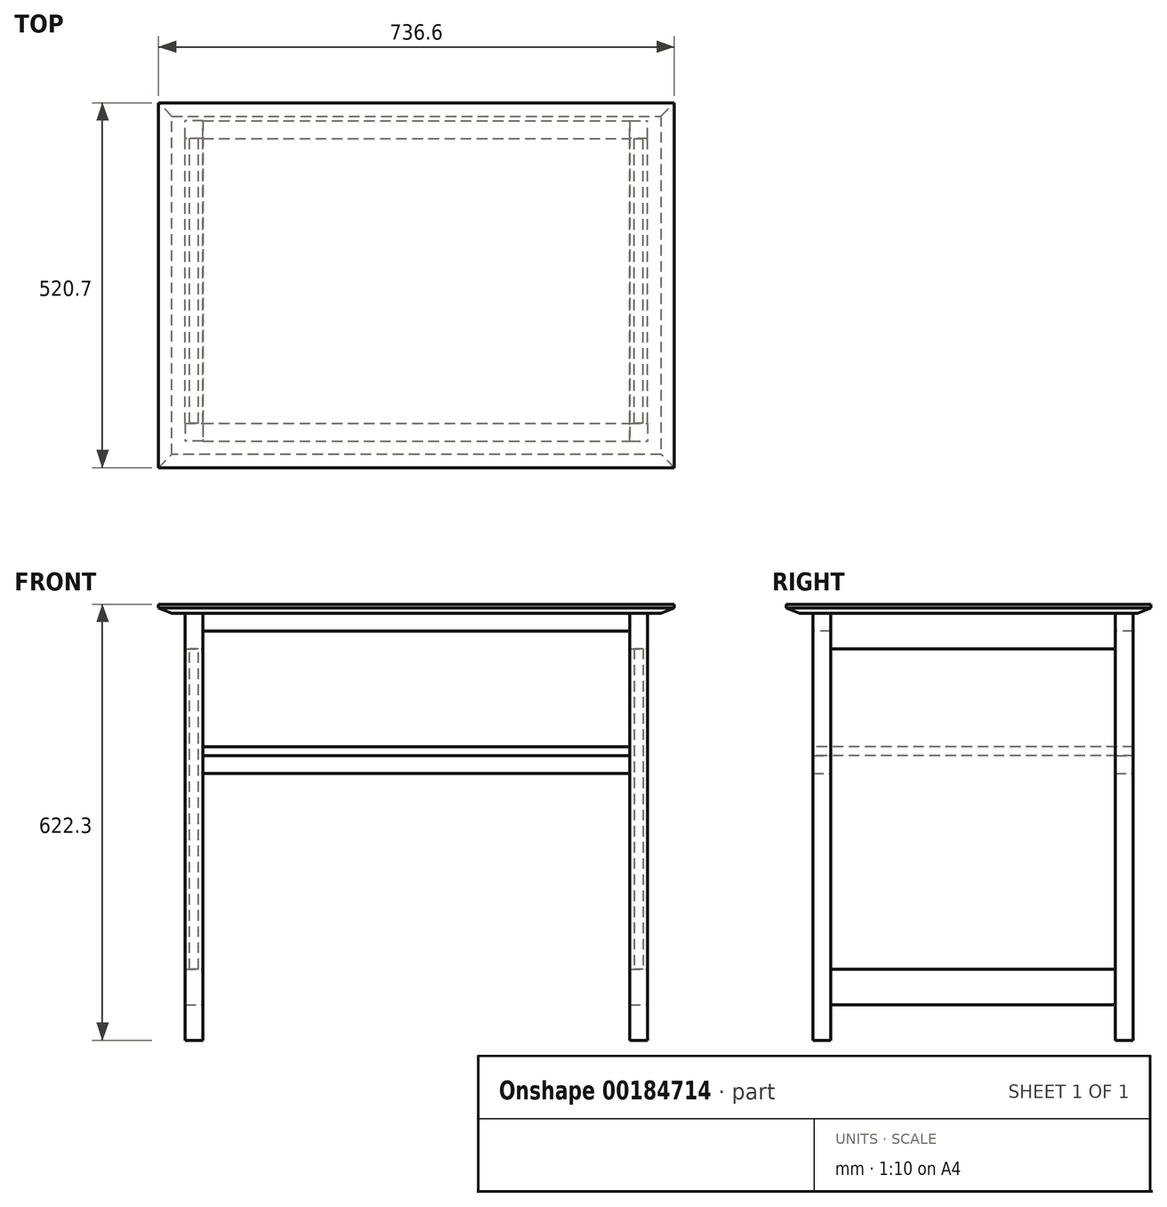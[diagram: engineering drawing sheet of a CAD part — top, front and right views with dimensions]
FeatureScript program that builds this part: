
annotation { "Feature Type Name" : "Feature", "Feature Type Description" : "" }
export const myFeature = defineFeature(function(context is Context, id is Id, definition is map)
    precondition{}
    {
        {
            var Q0;
            Q0=qCreatedBy(makeId("Top.planeOp"),FACE);
            var sketch = newSketch(context, id + "F0", { "sketchPlane" : qUnion([Q0])});
            skLineSegment(sketch, "E0.bottom", {"start": v(-304.8, 203.2) * mm, "end": v(304.8, 203.2) * mm});
            skLineSegment(sketch, "E0.top", {"start": v(-304.8, -203.2) * mm, "end": v(304.8, -203.2) * mm});
            skLineSegment(sketch, "E0.left", {"start": v(-304.8, 203.2) * mm, "end": v(-304.8, -203.2) * mm});
            skLineSegment(sketch, "E0.right", {"start": v(304.8, 203.2) * mm, "end": v(304.8, -203.2) * mm});
            skPoint(sketch, "E0.middle", {"position": v(0, 0) * mm});
            skLineSegment(sketch, "E1", {"start": v(0, 0) * mm, "end": v(0, 203.2) * mm});
            skLineSegment(sketch, "E2", {"start": v(0, 0) * mm, "end": v(-304.8, 0) * mm});
            skLineSegment(sketch, "E3.bottom", {"start": v(-304.8, 203.2) * mm, "end": v(-330.2, 203.2) * mm});
            skLineSegment(sketch, "E3.top", {"start": v(-304.8, 228.6) * mm, "end": v(-330.2, 228.6) * mm});
            skLineSegment(sketch, "E3.left", {"start": v(-304.8, 203.2) * mm, "end": v(-304.8, 228.6) * mm});
            skLineSegment(sketch, "E3.right", {"start": v(-330.2, 203.2) * mm, "end": v(-330.2, 228.6) * mm});
            skPoint(sketch, "E3.middle", {"position": v(-317.5, 215.9) * mm});
            skLineSegment(sketch, "E4.MirrorCS", {"start": v(330.2, 203.2) * mm, "end": v(330.2, 228.6) * mm});
            skPoint(sketch, "E5.MirrorP", {"position": v(317.5, 215.9) * mm});
            skLineSegment(sketch, "E6.MirrorCS", {"start": v(304.8, 203.2) * mm, "end": v(330.2, 203.2) * mm});
            skLineSegment(sketch, "E7.MirrorCS", {"start": v(304.8, 203.2) * mm, "end": v(304.8, 228.6) * mm});
            skLineSegment(sketch, "E8.MirrorCS", {"start": v(304.8, 228.6) * mm, "end": v(330.2, 228.6) * mm});
            skPoint(sketch, "E9.MirrorP", {"position": v(-317.5, -215.9) * mm});
            skLineSegment(sketch, "E10.MirrorCS", {"start": v(304.8, -203.2) * mm, "end": v(304.8, -228.6) * mm});
            skLineSegment(sketch, "E11.MirrorCS", {"start": v(304.8, -203.2) * mm, "end": v(330.2, -203.2) * mm});
            skLineSegment(sketch, "E12.MirrorCS", {"start": v(304.8, -228.6) * mm, "end": v(330.2, -228.6) * mm});
            skLineSegment(sketch, "E13.MirrorCS", {"start": v(-304.8, -228.6) * mm, "end": v(-330.2, -228.6) * mm});
            skLineSegment(sketch, "E14.MirrorCS", {"start": v(330.2, -203.2) * mm, "end": v(330.2, -228.6) * mm});
            skLineSegment(sketch, "E15.MirrorCS", {"start": v(-304.8, -203.2) * mm, "end": v(-304.8, -228.6) * mm});
            skLineSegment(sketch, "E16.MirrorCS", {"start": v(-304.8, -203.2) * mm, "end": v(-330.2, -203.2) * mm});
            skLineSegment(sketch, "E17.MirrorCS", {"start": v(-330.2, -203.2) * mm, "end": v(-330.2, -228.6) * mm});
            skPoint(sketch, "E18.MirrorP", {"position": v(317.5, -215.9) * mm});
            skSolve(sketch);
        }
        {
            var Q0;
            Q0=makeQuery(id+"F0.imprint","IMPRINT",FACE,{"disambiguationData":[TD([[makeQuery(id+"F0.imprint","IMPRINT",EDGE,{"derivedFrom":sQuery(id+"F0.wireOp",EDGE,"E3.bottom")}),-1.0]])]});
            var Q1;
            Q1=makeQuery(id+"F0.imprint","IMPRINT",FACE,{"disambiguationData":[TD([[makeQuery(id+"F0.imprint","IMPRINT",EDGE,{"derivedFrom":sQuery(id+"F0.wireOp",EDGE,"E4.MirrorCS")}),1.0]])]});
            var Q2;
            Q2=makeQuery(id+"F0.imprint","IMPRINT",FACE,{"disambiguationData":[TD([[makeQuery(id+"F0.imprint","IMPRINT",EDGE,{"derivedFrom":sQuery(id+"F0.wireOp",EDGE,"E10.MirrorCS")}),1.0]])]});
            var Q3;
            Q3=makeQuery(id+"F0.imprint","IMPRINT",FACE,{"disambiguationData":[TD([[makeQuery(id+"F0.imprint","IMPRINT",EDGE,{"derivedFrom":sQuery(id+"F0.wireOp",EDGE,"E13.MirrorCS")}),-1.0]])]});
            extrude(context, id + "F1", {"entities" : qUnion([Q0, Q1, Q2, Q3]), "depth" : 609.6 * mm});
        }
        {
            var Q0;
            Q0=makeQuery(id+"F1.opExtrude","SWEPT_FACE",FACE,{"disambiguationData":[OSD([sQuery(id+"F0.wireOp",EDGE,"E3.bottom")])]});
            var sketch = newSketch(context, id + "F2", { "sketchPlane" : qUnion([Q0])});
            skLineSegment(sketch, "E19.bottom", {"start": v(-330.2, 609.6) * mm, "end": v(-304.8, 609.6) * mm});
            skLineSegment(sketch, "E19.top", {"start": v(-330.2, 558.8) * mm, "end": v(-304.8, 558.8) * mm});
            skLineSegment(sketch, "E19.left", {"start": v(-330.2, 609.6) * mm, "end": v(-330.2, 558.8) * mm});
            skLineSegment(sketch, "E19.right", {"start": v(-304.8, 609.6) * mm, "end": v(-304.8, 558.8) * mm});
            skLineSegment(sketch, "E20.bottom", {"start": v(-330.2, 50.8) * mm, "end": v(-304.8, 50.8) * mm});
            skLineSegment(sketch, "E20.top", {"start": v(-330.2, 101.6) * mm, "end": v(-304.8, 101.6) * mm});
            skLineSegment(sketch, "E20.left", {"start": v(-330.2, 50.8) * mm, "end": v(-330.2, 101.6) * mm});
            skLineSegment(sketch, "E20.right", {"start": v(-304.8, 50.8) * mm, "end": v(-304.8, 101.6) * mm});
            skLineSegment(sketch, "E21", {"start": v(0, 0) * mm, "end": v(0, 145.1) * mm});
            skLineSegment(sketch, "E22.MirrorCS", {"start": v(330.2, 609.6) * mm, "end": v(304.8, 609.6) * mm});
            skLineSegment(sketch, "E23.MirrorCS", {"start": v(330.2, 50.8) * mm, "end": v(304.8, 50.8) * mm});
            skLineSegment(sketch, "E24.MirrorCS", {"start": v(330.2, 558.8) * mm, "end": v(304.8, 558.8) * mm});
            skLineSegment(sketch, "E25.MirrorCS", {"start": v(330.2, 101.6) * mm, "end": v(304.8, 101.6) * mm});
            skLineSegment(sketch, "E26.MirrorCS", {"start": v(304.8, 609.6) * mm, "end": v(304.8, 558.8) * mm});
            skLineSegment(sketch, "E27.MirrorCS", {"start": v(304.8, 50.8) * mm, "end": v(304.8, 101.6) * mm});
            skLineSegment(sketch, "E28.MirrorCS", {"start": v(330.2, 609.6) * mm, "end": v(330.2, 558.8) * mm});
            skLineSegment(sketch, "E29.MirrorCS", {"start": v(330.2, 50.8) * mm, "end": v(330.2, 101.6) * mm});
            skSolve(sketch);
        }
        {
            var Q0;
            Q0=makeQuery(id+"F2.imprint","IMPRINT",FACE,{"disambiguationData":[TD([[makeQuery(id+"F2.imprint","IMPRINT",EDGE,{"derivedFrom":sQuery(id+"F2.wireOp",EDGE,"E19.bottom")}),1.0]])]});
            var Q1;
            Q1=makeQuery(id+"F2.imprint","IMPRINT",FACE,{"disambiguationData":[TD([[makeQuery(id+"F2.imprint","IMPRINT",EDGE,{"derivedFrom":sQuery(id+"F2.wireOp",EDGE,"E22.MirrorCS")}),1.0]])]});
            var Q2;
            Q2=makeQuery(id+"F2.imprint","IMPRINT",FACE,{"disambiguationData":[TD([[makeQuery(id+"F2.imprint","IMPRINT",EDGE,{"derivedFrom":sQuery(id+"F2.wireOp",EDGE,"E23.MirrorCS")}),-1.0]])]});
            var Q3;
            Q3=makeQuery(id+"F2.imprint","IMPRINT",FACE,{"disambiguationData":[TD([[makeQuery(id+"F2.imprint","IMPRINT",EDGE,{"derivedFrom":sQuery(id+"F2.wireOp",EDGE,"E20.bottom")}),1.0]])]});
            extrude(context, id + "F3", {"entities" : qUnion([Q0, Q1, Q2, Q3]), "endBound" : BoundingType.UP_TO_NEXT, "depth" : 25.4 * mm});
        }
        {
            var Q0;
            Q0=makeQuery(id+"F1.opExtrude","SWEPT_FACE",FACE,{"disambiguationData":[OSD([sQuery(id+"F0.wireOp",EDGE,"E3.bottom")])]});
            var sketch = newSketch(context, id + "F4", { "sketchPlane" : qUnion([Q0])});
            skLineSegment(sketch, "E30.bottom", {"start": v(-311.15, 101.6) * mm, "end": v(-323.85, 101.6) * mm});
            skLineSegment(sketch, "E30.top", {"start": v(-311.15, 558.8) * mm, "end": v(-323.85, 558.8) * mm});
            skLineSegment(sketch, "E30.left", {"start": v(-311.15, 101.6) * mm, "end": v(-311.15, 558.8) * mm});
            skLineSegment(sketch, "E30.right", {"start": v(-323.85, 101.6) * mm, "end": v(-323.85, 558.8) * mm});
            skPoint(sketch, "E30.middle", {"position": v(-317.5, 330.2) * mm});
            skLineSegment(sketch, "E31", {"start": v(0, 0) * mm, "end": v(0, 207.5) * mm});
            skLineSegment(sketch, "E32.MirrorCS", {"start": v(311.15, 101.6) * mm, "end": v(323.85, 101.6) * mm});
            skLineSegment(sketch, "E33.MirrorCS", {"start": v(311.15, 558.8) * mm, "end": v(323.85, 558.8) * mm});
            skLineSegment(sketch, "E34.MirrorCS", {"start": v(323.85, 101.6) * mm, "end": v(323.85, 558.8) * mm});
            skLineSegment(sketch, "E35.MirrorCS", {"start": v(311.15, 101.6) * mm, "end": v(311.15, 558.8) * mm});
            skPoint(sketch, "E36.MirrorP", {"position": v(317.5, 330.2) * mm});
            skSolve(sketch);
        }
        {
            var Q0;
            Q0=makeQuery(id+"F4.imprint","IMPRINT",FACE,{"disambiguationData":[TD([[makeQuery(id+"F4.imprint","IMPRINT",EDGE,{"derivedFrom":sQuery(id+"F4.wireOp",EDGE,"E32.MirrorCS")}),1.0]])]});
            var Q1;
            Q1=makeQuery(id+"F4.imprint","IMPRINT",FACE,{"disambiguationData":[TD([[makeQuery(id+"F4.imprint","IMPRINT",EDGE,{"derivedFrom":sQuery(id+"F4.wireOp",EDGE,"E30.bottom")}),-1.0]])]});
            extrude(context, id + "F5", {"entities" : qUnion([Q0, Q1]), "endBound" : BoundingType.UP_TO_NEXT, "depth" : 25.4 * mm});
        }
        {
            var Q0;
            Q0=makeQuery(id+"F1.opExtrude","SWEPT_FACE",FACE,{"disambiguationData":[OSD([sQuery(id+"F0.wireOp",EDGE,"E10.MirrorCS")])]});
            var sketch = newSketch(context, id + "F6", { "sketchPlane" : qUnion([Q0])});
            skLineSegment(sketch, "E37.bottom", {"start": v(203.2, 406.4) * mm, "end": v(228.6, 406.4) * mm});
            skLineSegment(sketch, "E37.top", {"start": v(203.2, 381) * mm, "end": v(228.6, 381) * mm});
            skLineSegment(sketch, "E37.left", {"start": v(203.2, 406.4) * mm, "end": v(203.2, 381) * mm});
            skLineSegment(sketch, "E37.right", {"start": v(228.6, 406.4) * mm, "end": v(228.6, 381) * mm});
            skLineSegment(sketch, "E38.bottom", {"start": v(-203.2, 381) * mm, "end": v(-228.6, 381) * mm});
            skLineSegment(sketch, "E38.top", {"start": v(-203.2, 406.4) * mm, "end": v(-228.6, 406.4) * mm});
            skLineSegment(sketch, "E38.left", {"start": v(-203.2, 381) * mm, "end": v(-203.2, 406.4) * mm});
            skLineSegment(sketch, "E38.right", {"start": v(-228.6, 381) * mm, "end": v(-228.6, 406.4) * mm});
            skLineSegment(sketch, "E39.bottom", {"start": v(228.6, 609.6) * mm, "end": v(203.2, 609.6) * mm});
            skLineSegment(sketch, "E39.top", {"start": v(228.6, 584.2) * mm, "end": v(203.2, 584.2) * mm});
            skLineSegment(sketch, "E39.left", {"start": v(228.6, 609.6) * mm, "end": v(228.6, 584.2) * mm});
            skLineSegment(sketch, "E39.right", {"start": v(203.2, 609.6) * mm, "end": v(203.2, 584.2) * mm});
            skLineSegment(sketch, "E40.bottom", {"start": v(-228.6, 609.6) * mm, "end": v(-203.2, 609.6) * mm});
            skLineSegment(sketch, "E40.top", {"start": v(-228.6, 584.2) * mm, "end": v(-203.2, 584.2) * mm});
            skLineSegment(sketch, "E40.left", {"start": v(-228.6, 609.6) * mm, "end": v(-228.6, 584.2) * mm});
            skLineSegment(sketch, "E40.right", {"start": v(-203.2, 609.6) * mm, "end": v(-203.2, 584.2) * mm});
            skSolve(sketch);
        }
        {
            var Q0;
            Q0=makeQuery(id+"F6.imprint","IMPRINT",FACE,{"disambiguationData":[TD([[makeQuery(id+"F6.imprint","IMPRINT",EDGE,{"derivedFrom":sQuery(id+"F6.wireOp",EDGE,"E40.bottom")}),-1.0]])]});
            var Q1;
            Q1=makeQuery(id+"F6.imprint","IMPRINT",FACE,{"disambiguationData":[TD([[makeQuery(id+"F6.imprint","IMPRINT",EDGE,{"derivedFrom":sQuery(id+"F6.wireOp",EDGE,"E38.bottom")}),-1.0]])]});
            var Q2;
            Q2=makeQuery(id+"F6.imprint","IMPRINT",FACE,{"disambiguationData":[TD([[makeQuery(id+"F6.imprint","IMPRINT",EDGE,{"derivedFrom":sQuery(id+"F6.wireOp",EDGE,"E37.bottom")}),-1.0]])]});
            var Q3;
            Q3=makeQuery(id+"F6.imprint","IMPRINT",FACE,{"disambiguationData":[TD([[makeQuery(id+"F6.imprint","IMPRINT",EDGE,{"derivedFrom":sQuery(id+"F6.wireOp",EDGE,"E39.bottom")}),-1.0]])]});
            extrude(context, id + "F7", {"entities" : qUnion([Q0, Q1, Q2, Q3]), "endBound" : BoundingType.UP_TO_NEXT, "depth" : 25.4 * mm});
        }
        {
            var Q0;
            Q0=makeQuery(id+"F7.opExtrude","SWEPT_FACE",FACE,{"disambiguationData":[OSD([sQuery(id+"F6.wireOp",EDGE,"E37.right")])]});
            var sketch = newSketch(context, id + "F8", { "sketchPlane" : qUnion([Q0])});
            skLineSegment(sketch, "E41.bottom", {"start": v(-304.8, 406.4) * mm, "end": v(304.8, 406.4) * mm});
            skLineSegment(sketch, "E41.top", {"start": v(-304.8, 419.1) * mm, "end": v(304.8, 419.1) * mm});
            skLineSegment(sketch, "E41.left", {"start": v(-304.8, 406.4) * mm, "end": v(-304.8, 419.1) * mm});
            skLineSegment(sketch, "E41.right", {"start": v(304.8, 406.4) * mm, "end": v(304.8, 419.1) * mm});
            skSolve(sketch);
        }
        {
            var Q0;
            Q0=makeQuery(id+"F8.imprint","IMPRINT",FACE,{"disambiguationData":[TD([[makeQuery(id+"F8.imprint","IMPRINT",EDGE,{"derivedFrom":sQuery(id+"F8.wireOp",EDGE,"E41.bottom")}),1.0]])]});
            var Q1;
            Q1=makeQuery(id+"F1.opExtrude","SWEPT_FACE",FACE,{"disambiguationData":[OSD([sQuery(id+"F0.wireOp",EDGE,"E3.top")])]});
            extrude(context, id + "F9", {"entities" : qUnion([Q0]), "endBound" : BoundingType.UP_TO_SURFACE, "oppositeDirection" : true, "endBoundEntityFace" : qUnion([Q1]), "depth" : 25.4 * mm});
        }
        {
            var Q0;
            Q0=makeQuery(id+"F3.opExtrude","SWEPT_FACE",FACE,{"disambiguationData":[OSD([sQuery(id+"F2.wireOp",EDGE,"E19.bottom")])]});
            var sketch = newSketch(context, id + "F10", { "sketchPlane" : qUnion([Q0])});
            skLineSegment(sketch, "E42.bottom", {"start": v(-368.3, 254) * mm, "end": v(368.3, 254) * mm});
            skLineSegment(sketch, "E42.top", {"start": v(-368.3, -266.7) * mm, "end": v(368.3, -266.7) * mm});
            skLineSegment(sketch, "E42.left", {"start": v(-368.3, 254) * mm, "end": v(-368.3, -266.7) * mm});
            skLineSegment(sketch, "E42.right", {"start": v(368.3, 254) * mm, "end": v(368.3, -266.7) * mm});
            skSolve(sketch);
        }
        {
            var Q0;
            Q0=makeQuery(id+"F10.imprint","IMPRINT",FACE,{"disambiguationData":[TD([[makeQuery(id+"F10.imprint","IMPRINT",EDGE,{"derivedFrom":sQuery(id+"F10.wireOp",EDGE,"E42.bottom")}),-1.0]])]});
            var Q1;
            {var subQ0=sQuery(id+"F2.wireOp",EDGE,"E19.bottom");Q1=makeQuery(id+"F10.imprint","IMPRINT",FACE,{"disambiguationData":[TD([[makeQuery(id+"F10.imprint","IMPRINT",EDGE,{"derivedFrom":makeQuery(id+"F3.opExtrude","CAP_EDGE",EDGE,{"disambiguationData":[OSD([subQ0])],"isStart":true})}),1.0]])]});}
            extrude(context, id + "F11", {"entities" : qUnion([Q0, Q1]), "depth" : 12.7 * mm});
        }
        {
            var Q0;
            Q0=makeQuery(id+"F11.opExtrude","CAP_EDGE",EDGE,{"disambiguationData":[OSD([sQuery(id+"F10.wireOp",EDGE,"E42.top")])],"isStart":true});
            var Q1;
            Q1=makeQuery(id+"F11.opExtrude","CAP_EDGE",EDGE,{"disambiguationData":[OSD([sQuery(id+"F10.wireOp",EDGE,"E42.left")])],"isStart":true});
            var Q2;
            Q2=makeQuery(id+"F11.opExtrude","CAP_EDGE",EDGE,{"disambiguationData":[OSD([sQuery(id+"F10.wireOp",EDGE,"E42.right")])],"isStart":true});
            var Q3;
            Q3=makeQuery(id+"F11.opExtrude","CAP_EDGE",EDGE,{"disambiguationData":[OSD([sQuery(id+"F10.wireOp",EDGE,"E42.bottom")])],"isStart":true});
            chamfer(context, id + "F12", {"entities" : qUnion([Q0, Q1, Q2, Q3]), "chamferType" : ChamferType.TWO_OFFSETS, "width1" : 7.62 * mm, "oppositeDirection" : false, "width2" : 19.05 * mm, "tangentPropagation" : true});
        }
    });
